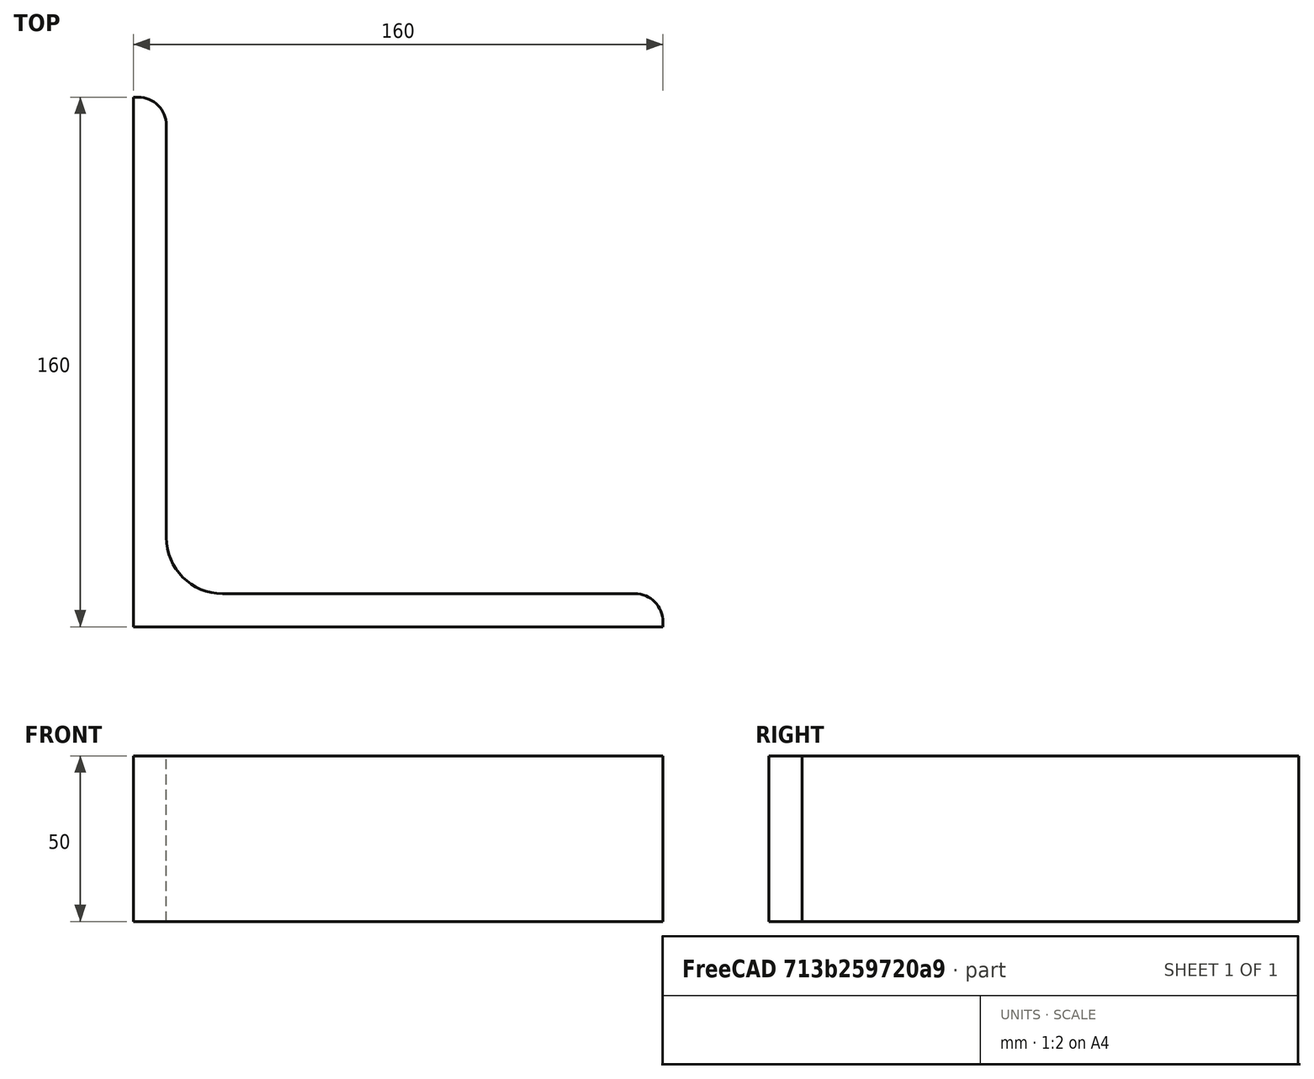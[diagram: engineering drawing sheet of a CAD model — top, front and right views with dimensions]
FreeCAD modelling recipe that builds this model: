
FCSTD DOCUMENT  (FreeCAD 0.15R4671 (Git))
Label: Angle Bar L160x160x10 EN10056 S235JR
License: All rights reserved
LicenseURL: http://en.wikipedia.org/wiki/All_rights_reserved
objects: Sketcher::SketchObject×1, Part::Extrusion×1
note: 2 computed .brp shape members not serialized (recipe doc carries the construction recipe); baked Part::Feature solids carry a one-line shape summary decoded from their .brp

FEATURE [Sketcher::SketchObject] Sketch
  sketch-geometry (9):
    g0: LineSegment StartX=0 StartY=0 StartZ=0 EndX=160 EndY=0 EndZ=0
    g1: LineSegment StartX=160 StartY=0 StartZ=0 EndX=160 EndY=1.5 EndZ=0
    g2: LineSegment StartX=151.5 StartY=10 StartZ=0 EndX=27 EndY=10 EndZ=0
    g3: LineSegment StartX=0 StartY=0 StartZ=0 EndX=0 EndY=160 EndZ=0
    g4: LineSegment StartX=0 StartY=160 StartZ=0 EndX=1.5 EndY=160 EndZ=0
    g5: LineSegment StartX=10 StartY=151.5 StartZ=0 EndX=10 EndY=27 EndZ=0
    g6: ArcOfCircle CenterX=27 CenterY=27 CenterZ=0 NormalX=0 NormalY=0 NormalZ=1 Radius=17 StartAngle=3.14159 EndAngle=4.71239
    g7: ArcOfCircle CenterX=1.5 CenterY=151.5 CenterZ=0 NormalX=0 NormalY=0 NormalZ=1 Radius=8.5 StartAngle=0 EndAngle=1.5708
    g8: ArcOfCircle CenterX=151.5 CenterY=1.5 CenterZ=0 NormalX=0 NormalY=0 NormalZ=1 Radius=8.5 StartAngle=0 EndAngle=1.5708
  constraints (23):
    c: Coincident(g0,g-1)
    c: Horizontal(g0)
    c: Coincident(g1,g0)
    c: Vertical(g1)
    c: Horizontal(g2)
    c: Coincident(g3,g-1)
    c: Vertical(g3)
    c: Coincident(g4,g3)
    c: Horizontal(g4)
    c: Vertical(g5)
    c: Tangent(g5,g6) = -1.5708
    c: Tangent(g2,g6) = 1.5708
    c: Tangent(g4,g7) = 1.5708
    c: Tangent(g5,g7) = 1.5708
    c: Tangent(g2,g8) = -1.5708
    c: Tangent(g1,g8) = -1.5708
    c: DistanceX(g0) = 160
    c: DistanceY(g3) = 160
    c: DistanceY(g0,g2) = 10
    c: DistanceX(g3,g5) = 10
    c: Radius(g6) = 17
    c: Radius(g8) = 8.5
    c: Radius(g7) = 8.5
FEATURE [Part::Extrusion] Extrude  label="Angle Bar L160x160x10 EN10056 S235JR"
  Base = -> Sketch
  Dir = (0,0,50)
  Solid = true
